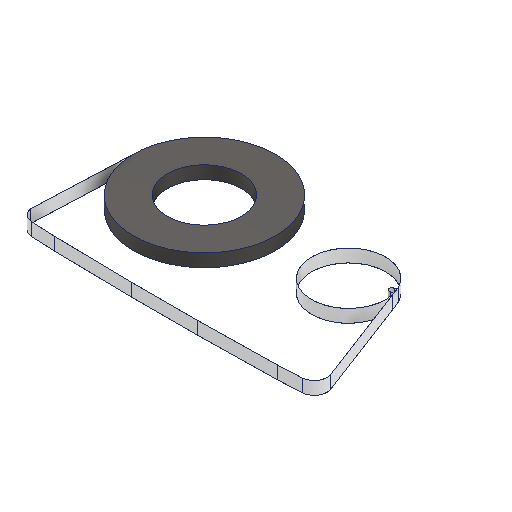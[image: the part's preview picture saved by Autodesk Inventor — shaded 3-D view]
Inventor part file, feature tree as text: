
AUTODESK INVENTOR PART (.ipt)
format: ipt  version: 2022 (Build 260153000, 153)  size: 141,312 bytes
history: native  units: mm
features: other x1, extrude x1
ambient origin geometry x8: Origin, YZ Plane, XZ Plane, XY Plane, X Axis, Y Axis, Z Axis, Center Point
bodies: Volumenkörper1 (feature_tree), Volumenkörper2 (feature_tree)
feature tree (2):
  other  "Boss-Extrude1"
  extrude  "Extrude-Thin1"  [1 undecoded]
note: 1 required parameter value undecoded (feature->parameter linkage not recoverable at this tier; creation-order binding heuristic only, values carry confidence <= 0.55)
